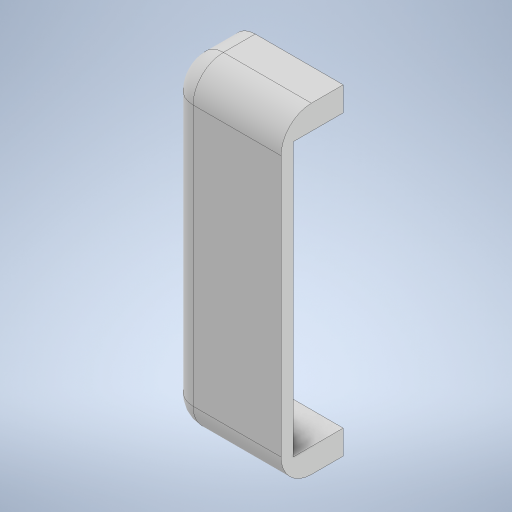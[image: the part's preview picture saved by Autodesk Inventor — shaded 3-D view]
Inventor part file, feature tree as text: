
AUTODESK INVENTOR PART (.ipt)
format: ipt  version: 2023 (Build 270158000, 158)  size: 358,912 bytes
history: native  units: in
note: dims shown in document units (in); Inventor stores cm internally (conversion verified against a paired STEP export)
features: reference x12, other x6, sketch x6, projected_geometry x6, extrude x5, fillet x2, hole x1
ambient origin geometry x8: Origin, YZ Plane, XZ Plane, XY Plane, X Axis, Y Axis, Z Axis, Center Point
bodies: Body1 (feature_tree)
feature tree (38):
  other  "Bryła1"
  sketch  "Szkic1"
  other  "Płaszczyzna konstrukcyjna1"
  extrude  "Wyciągnięcie proste1"  Depth=0.1575in
  extrude  "Wyciągnięcie proste2"  Depth=0.1575in
  hole  "Otwór1"  [1 undecoded]
  extrude  "Wyciągnięcie proste3"  Depth=0.0787in TaperAngle=0.0deg
  fillet  "Zaokrąglenie1"  Radius=0.0787in
  extrude  "Wyciągnięcie proste4"  Depth=0.0787in
  fillet  "Zaokrąglenie2"  Radius=0.0984in
  extrude  "Wyciągnięcie proste5"  Depth=0.0984in
  reference  "Odniesienie1"
  reference  "Odniesienie2"
  reference  "Odniesienie3"
  reference  "Odniesienie4"
  reference  "Odniesienie5"
  reference  "Odniesienie6"
  reference  "Odniesienie7"
  reference  "Odniesienie8"
  reference  "Odniesienie9"
  reference  "Odniesienie10"
  reference  "Odniesienie11"
  reference  "Odniesienie12"
  sketch  "Szkic2"
  projected_geometry  "Pętla rzutowana1"
  projected_geometry  "Pętla rzutowana2"
  projected_geometry  "Pętla rzutowana3"
  sketch  "Szkic3"
  sketch  "Szkic4"
  projected_geometry  "Pętla rzutowana4"
  sketch  "Szkic5"
  projected_geometry  "Pętla rzutowana5"
  sketch  "Szkic6"
  projected_geometry  "Pętla rzutowana6"
  other  "<userpath>\Desktop\MojeRoboty\Stefan\mechanics 2\STEFAN.iam"
  other  "STEFAN.iam"
  other  "servo_mini_1370hd_cos:1"
  other  "servo_mini_1370hd_cos:2"
note: 1 required parameter value undecoded (feature->parameter linkage not recoverable at this tier; creation-order binding heuristic only, values carry confidence <= 0.55)
